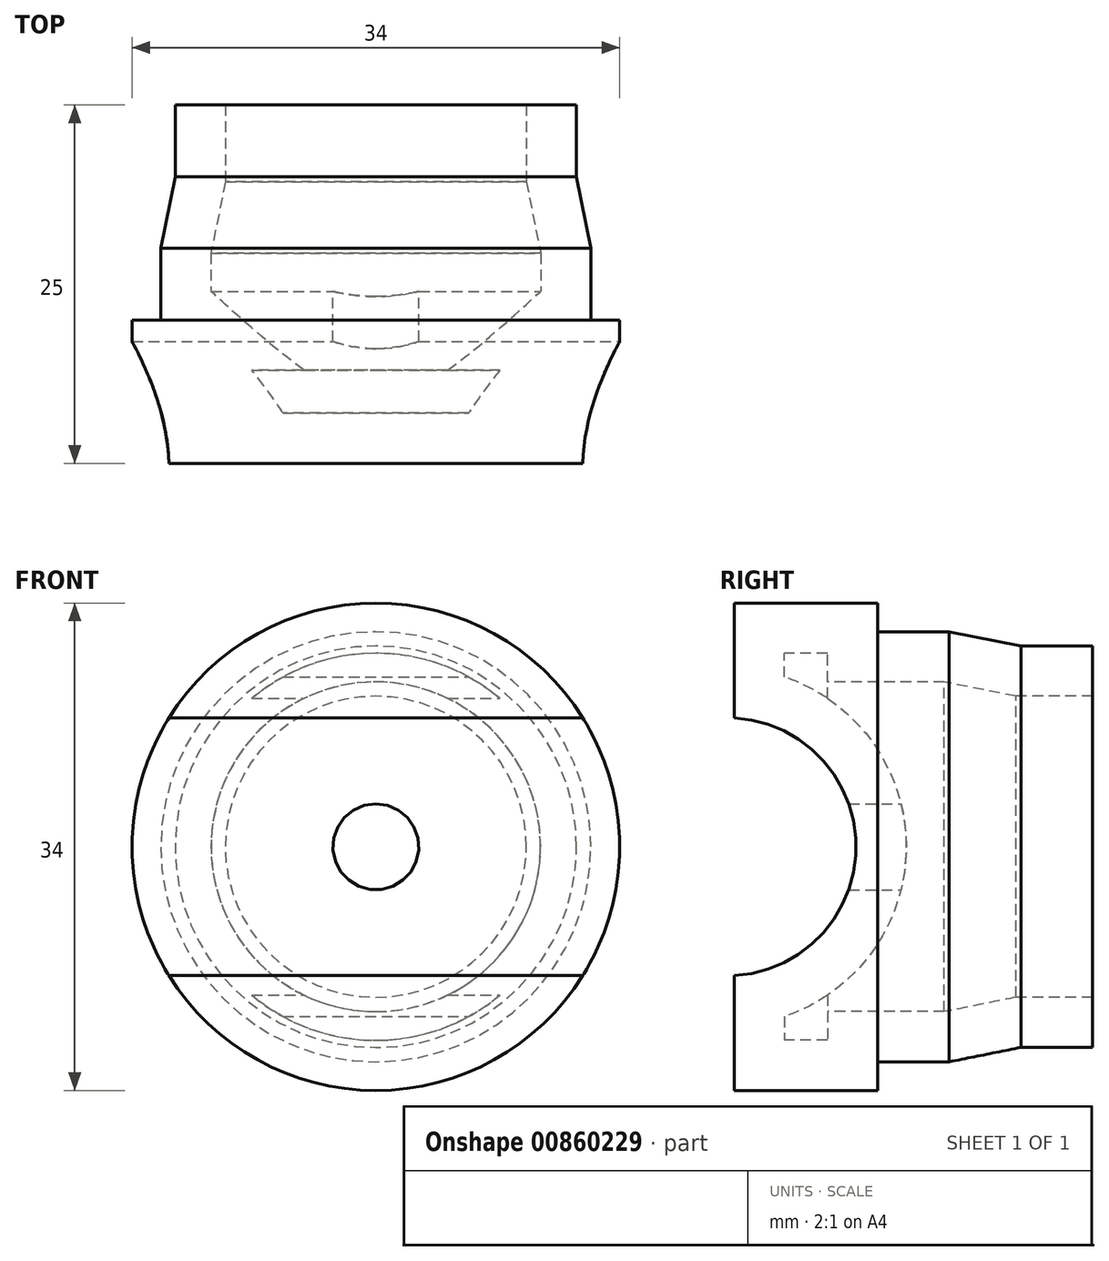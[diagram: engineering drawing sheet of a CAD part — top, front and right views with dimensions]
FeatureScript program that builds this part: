
annotation { "Feature Type Name" : "Feature", "Feature Type Description" : "" }
export const myFeature = defineFeature(function(context is Context, id is Id, definition is map)
    precondition{}
    {
        {
            var Q0;
            Q0=qCreatedBy(makeId("Right.planeOp"),FACE);
            var sketch = newSketch(context, id + "F0", { "sketchPlane" : qUnion([Q0])});
            skLineSegment(sketch, "E0", {"start": v(25, 0) * mm, "end": v(25, 14) * mm});
            skLineSegment(sketch, "E1", {"start": v(25, 14) * mm, "end": v(20, 14) * mm});
            skLineSegment(sketch, "E2", {"start": v(20, 14) * mm, "end": v(15, 15) * mm});
            skLineSegment(sketch, "E3", {"start": v(15, 15) * mm, "end": v(10, 15) * mm});
            skLineSegment(sketch, "E4", {"start": v(10, 15) * mm, "end": v(10, 17) * mm});
            skLineSegment(sketch, "E5", {"start": v(10, 17) * mm, "end": v(0, 17) * mm});
            skLineSegment(sketch, "E6", {"start": v(0, 17) * mm, "end": v(0, 0) * mm});
            skLineSegment(sketch, "E7", {"start": v(0, 0) * mm, "end": v(25, 0) * mm});
            skSolve(sketch);
        }
        {
            var Q0;
            Q0=makeQuery(id+"F0.imprint","IMPRINT",FACE,{"disambiguationData":[TD([[makeQuery(id+"F0.imprint","IMPRINT",EDGE,{"derivedFrom":sQuery(id+"F0.wireOp",EDGE,"E0")}),1.0]])]});
            var Q1;
            Q1=sQuery(id+"F0.wireOp",EDGE,"E7");
            revolve(context, id + "F1", {"surfaceOperationType" : NewSurfaceOperationType.NEW, "entities" : qUnion([Q0]), "axis" : qUnion([Q1]), "revolveType" : RevolveType.FULL});
        }
        {
            var Q0;
            Q0=qCreatedBy(makeId("Right.planeOp"),FACE);
            var sketch = newSketch(context, id + "F2", { "sketchPlane" : qUnion([Q0])});
            skCircle(sketch, "E8", {"center": v(-0.5, 0) * mm, "radius": 9 * mm});
            skSolve(sketch);
        }
        {
            var Q0;
            Q0=makeQuery(id+"F2.imprint","IMPRINT",FACE,{"disambiguationData":[TD([[makeQuery(id+"F2.imprint","IMPRINT",EDGE,{"derivedFrom":sQuery(id+"F2.wireOp",EDGE,"E8")}),1.0]])]});
            extrude(context, id + "F3", {"entities" : qUnion([Q0]), "operationType" : NewBodyOperationType.REMOVE, "endBound" : BoundingType.SYMMETRIC, "oppositeDirection" : true, "depth" : 50 * mm, "offsetDistance" : 25 * mm});
        }
        {
            var Q0;
            Q0=makeQuery(id+"F1.opRevolve","SWEPT_FACE",FACE,{"disambiguationData":[OSD([sQuery(id+"F0.wireOp",EDGE,"E0")])]});
            var sketch = newSketch(context, id + "F4", { "sketchPlane" : qUnion([Q0])});
            skPoint(sketch, "E9", {"position": v(0, 0) * mm});
            skSolve(sketch);
        }
        {
            var Q0;
            Q0=makeQuery(id+"F1.opRevolve","SWEPT_FACE",FACE,{"disambiguationData":[OSD([sQuery(id+"F0.wireOp",EDGE,"E0")])]});
            shell(context, id + "F5", {"entities" : qUnion([Q0]), "thickness" : 3.5 * mm});
        }
        {
            var Q0;
            Q0=sQuery(id+"F4.wireOp",VERTEX,"E9");
            var Q1;
            Q1=makeQuery(id+"F1.opRevolve","SWEPT_BODY",BODY,{"disambiguationData":[OSD([sQuery(id+"F0.wireOp",EDGE,"E0"),sQuery(id+"F0.wireOp",EDGE,"E1"),sQuery(id+"F0.wireOp",EDGE,"E2"),sQuery(id+"F0.wireOp",EDGE,"E3"),sQuery(id+"F0.wireOp",EDGE,"E4"),sQuery(id+"F0.wireOp",EDGE,"E5"),sQuery(id+"F0.wireOp",EDGE,"E6"),sQuery(id+"F0.wireOp",EDGE,"E7")])]});
            hole(context, id + "F6", {"style" : HoleStyle.SIMPLE, "endStyle" : HoleEndStyle.THROUGH, "holeDiameter" : 6 * mm, "majorDiameter" : 5 * mm, "isTappedThrough" : true, "tappedDepth" : 12 * mm, "tapClearance" : 3, "locations" : qUnion([Q0]), "scope" : qUnion([Q1])});
        }
    });
